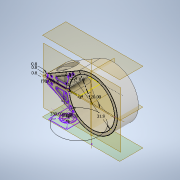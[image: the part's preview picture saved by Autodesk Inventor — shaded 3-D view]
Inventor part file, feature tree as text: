
AUTODESK INVENTOR PART (.ipt)
format: ipt  version: 2022 (Build 260153000, 153)  size: 422,912 bytes
history: native  units: mm
features: extrude x11, other x7, sketch x5, fillet x4, projected_geometry x4, mirror x2, hole x1
ambient origin geometry x8: Origin, YZ Plane, XZ Plane, XY Plane, X Axis, Y Axis, Z Axis, Center Point
bodies: Body1 (feature_tree)
feature tree (34):
  other  "ソリッド1"
  other  "baseScetcj"
  extrude  "押し出し1"  Depth=31.9mm
  sketch  "スケッチ2"
  sketch  "スケッチ3"
  other  "作業平面1"
  other  "m6hole"
  mirror  "ミラー1"
  other  "HexagonSC"
  extrude  "押し出し2"  Depth=2.0mm
  extrude  "押し出し3"  TaperAngle=120.0deg  [1 undecoded]
  extrude  "押し出し4"  TaperAngle=150.0deg  [1 undecoded]
  sketch  "スケッチ7"
  sketch  "スケッチ8"
  other  "sidescetch"
  extrude  "押し出し5"  Depth=2.0mm
  extrude  "押し出し6"  Depth=2.0mm
  extrude  "押し出し7"  Depth=2.4mm
  fillet  "フィレット1"  Radius=0.8mm
  fillet  "フィレット2"  Radius=0.8mm
  extrude  "Extrusion8"  Depth=0.8mm
  extrude  "Extrusion9"  Depth=15.0mm TaperAngle=0.0deg
  fillet  "Fillet3"  Radius=25.0mm
  fillet  "Fillet4"  Radius=6.4mm
  extrude  "Extrusion10"  Depth=11.5mm
  hole  "Hole1"  [1 undecoded]
  extrude  "Extrusion11"  TaperAngle=120.0deg  [1 undecoded]
  mirror  "Mirror2"
  projected_geometry  "投影ループ1"
  projected_geometry  "投影ループ2"
  projected_geometry  "投影ループ3"
  other  "作業平面2"
  sketch  "スケッチ6"
  projected_geometry  "投影ループ4"
note: 4 required parameter values undecoded (feature->parameter linkage not recoverable at this tier; creation-order binding heuristic only, values carry confidence <= 0.55)
